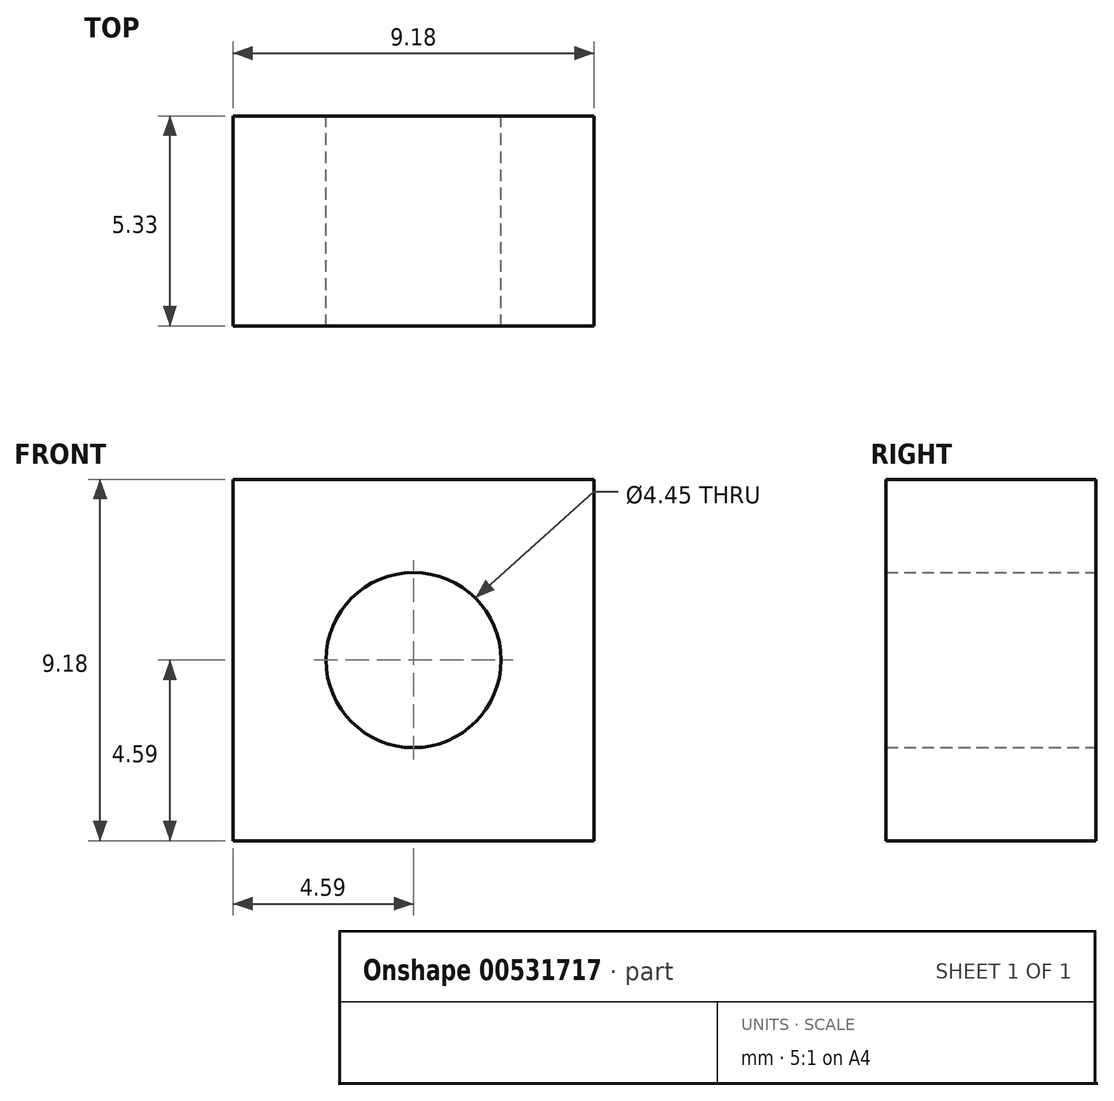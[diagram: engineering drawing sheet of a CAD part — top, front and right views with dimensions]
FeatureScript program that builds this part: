
annotation { "Feature Type Name" : "Feature", "Feature Type Description" : "" }
export const myFeature = defineFeature(function(context is Context, id is Id, definition is map)
    precondition{}
    {
        {
            var Q0;
            Q0=qCreatedBy(makeId("Front.planeOp"),FACE);
            var sketch = newSketch(context, id + "F0", { "sketchPlane" : qUnion([Q0])});
            skLineSegment(sketch, "E0.bottom", {"start": v(4.59, -4.59) * mm, "end": v(-4.59, -4.59) * mm});
            skLineSegment(sketch, "E0.top", {"start": v(4.59, 4.59) * mm, "end": v(-4.59, 4.59) * mm});
            skLineSegment(sketch, "E0.left", {"start": v(4.59, -4.59) * mm, "end": v(4.59, 4.59) * mm});
            skLineSegment(sketch, "E0.right", {"start": v(-4.59, -4.59) * mm, "end": v(-4.59, 4.59) * mm});
            skPoint(sketch, "E0.middle", {"position": v(0, 0) * mm});
            skCircle(sketch, "E1", {"center": v(0, 0) * mm, "radius": 2.22 * mm});
            skSolve(sketch);
        }
        {
            var Q0;
            Q0=makeQuery(id+"F0.imprint","IMPRINT",FACE,{"disambiguationData":[TD([[makeQuery(id+"F0.imprint","IMPRINT",EDGE,{"derivedFrom":sQuery(id+"F0.wireOp",EDGE,"E0.bottom")}),-1.0]])]});
            extrude(context, id + "F1", {"entities" : qUnion([Q0]), "depth" : 5.33 * mm, "offsetDistance" : 25.4 * mm});
        }
    });
